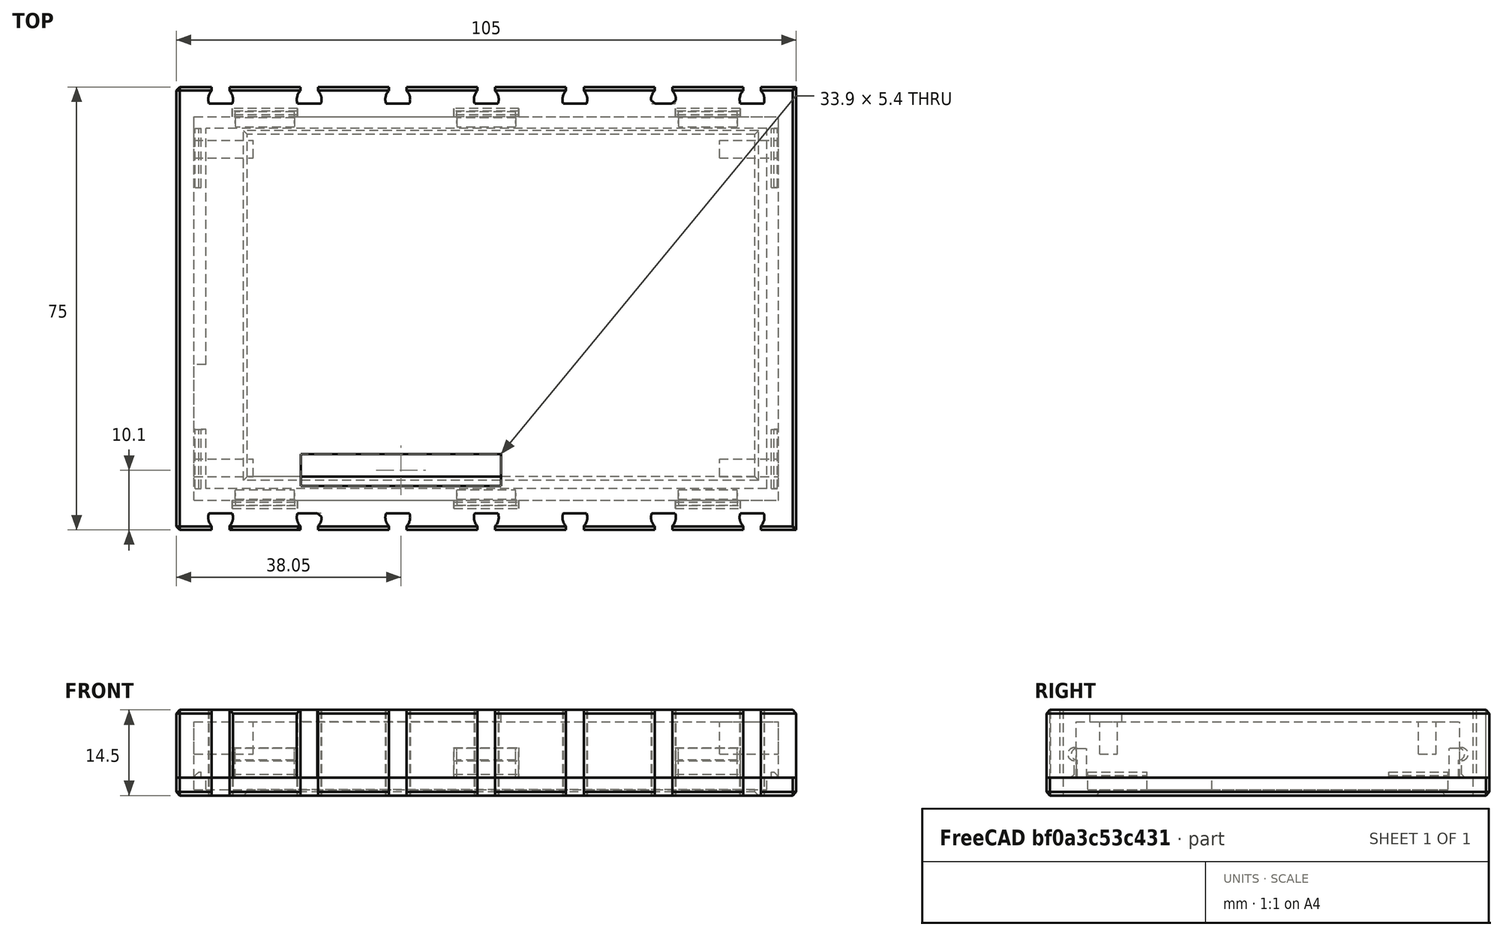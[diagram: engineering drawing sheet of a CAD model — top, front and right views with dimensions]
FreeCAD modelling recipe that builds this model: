
FCSTD DOCUMENT  (FreeCAD 0.19RUnknown)
Label: Display40
License: All rights reserved
LicenseURL: http://en.wikipedia.org/wiki/All_rights_reserved
objects: Part::Box×55, Part::MultiFuse×45, Part::Cylinder×26, Part::Cut×20, Part::Chamfer×3
note: 149 computed .brp shape members not serialized (recipe doc carries the construction recipe); baked Part::Feature solids carry a one-line shape summary decoded from their .brp

FEATURE [Part::Box] Box  label="Displ_base"
  AttacherType = Attacher::AttachEngine3D
  Height = 6
  Length = 95
  Width = 61
FEATURE [Part::Box] Box001  label="Connector"
  AttacherType = Attacher::AttachEngine3D
  Height = 13.4
  Length = 33.9
  Placement = pos=(16.1,0.4,6) rot=(0,0,1;0rad)
  Width = 5.4
FEATURE [Part::Box] Box002  label="Ribbon wire"
  AttacherType = Attacher::AttachEngine3D
  Height = 6
  Length = 2
  Placement = pos=(-2,10,0) rot=(0,0,1;0rad)
  Width = 11
FEATURE [Part::Box] Box003  label="Screen"
  AttacherType = Attacher::AttachEngine3D
  Height = 6
  Length = 86
  Placement = pos=(7,2,-3) rot=(0,0,1;0rad)
  Width = 58
FEATURE [Part::MultiFuse] Fusion  label="Display dummy"
  Shapes = -> [Box,Box001,Box003,Box002]
FEATURE [Part::Box] Box004  label="Displ_base001"
  AttacherType = Attacher::AttachEngine3D
  Height = 3
  Length = 105
  Placement = pos=(-5,-7,-1) rot=(0,0,1;0rad)
  Width = 75
FEATURE [Part::Cut] Cut
  Base = -> Box004
  Tool = -> Fusion
FEATURE [Part::Box] Box005  label="Displ_base002"
  AttacherType = Attacher::AttachEngine3D
  Height = 11.5
  Length = 105
  Placement = pos=(-5,-7,2) rot=(0,0,1;0rad)
  Width = 75
FEATURE [Part::Box] Box006  label="Displ_base003"
  AttacherType = Attacher::AttachEngine3D
  Height = 9.5
  Length = 99
  Placement = pos=(-2,-2,2) rot=(0,0,1;0rad)
  Width = 65
FEATURE [Part::Cut] Cut001
  Base = -> Box005
  Tool = -> Box006
FEATURE [Part::Cut] Cut002
  Base = -> Cut001
  Tool = -> Fusion
FEATURE [Part::Cylinder] Cylinder  label="bohrung"
  Angle = 360
  AttacherType = Attacher::AttachEngine3D
  Height = 25
  Placement = pos=(0,0,0) rot=(1,0,0;1.5708rad)
  Radius = 2.1
FEATURE [Part::Box] Box007  label="Nut 3x25x2"
  AttacherType = Attacher::AttachEngine3D
  Height = 2
  Length = 3
  Placement = pos=(6,0,0) rot=(0,0,1;0rad)
  Width = 25
FEATURE [Part::Box] Box008  label="Abflachung"
  AttacherType = Attacher::AttachEngine3D
  Height = 2
  Length = 4
  Placement = pos=(-2,-25,0.7) rot=(0,0,1;0rad)
  Width = 25
FEATURE [Part::Cut] Cut003  label="Kreisnut 4x25"
  Base = -> Cylinder
  Placement = pos=(7.5,25,2.1) rot=(0,0,1;0rad)
  Tool = -> Box008
FEATURE [Part::MultiFuse] Fusion001
  Placement = pos=(-5,68,-5) rot=(1,0,0;1.5708rad)
  Shapes = -> [Box007,Cut003]
FEATURE [Part::Box] Box009  label="Abflachung001"
  AttacherType = Attacher::AttachEngine3D
  Height = 2
  Length = 4
  Placement = pos=(-2,-25,0.7) rot=(0,0,1;0rad)
  Width = 25
FEATURE [Part::Box] Box010  label="Nut 3x25x003"
  AttacherType = Attacher::AttachEngine3D
  Height = 2
  Length = 3
  Placement = pos=(6,0,0) rot=(0,0,1;0rad)
  Width = 25
FEATURE [Part::Cylinder] Cylinder001  label="bohrung001"
  Angle = 360
  AttacherType = Attacher::AttachEngine3D
  Height = 25
  Placement = pos=(0,0,0) rot=(1,0,0;1.5708rad)
  Radius = 2.1
FEATURE [Part::Cut] Cut004  label="Kreisnut 4x026"
  Base = -> Cylinder001
  Placement = pos=(7.5,25,2.1) rot=(0,0,1;0rad)
  Tool = -> Box009
FEATURE [Part::MultiFuse] Fusion002
  Placement = pos=(10,68,-5) rot=(1,0,0;1.5708rad)
  Shapes = -> [Box010,Cut004]
FEATURE [Part::Box] Box011  label="Abflachung002"
  AttacherType = Attacher::AttachEngine3D
  Height = 2
  Length = 4
  Placement = pos=(-2,-25,0.7) rot=(0,0,1;0rad)
  Width = 25
FEATURE [Part::Box] Box012  label="Nut 3x25x004"
  AttacherType = Attacher::AttachEngine3D
  Height = 2
  Length = 3
  Placement = pos=(6,0,0) rot=(0,0,1;0rad)
  Width = 25
FEATURE [Part::Cylinder] Cylinder002  label="bohrung002"
  Angle = 360
  AttacherType = Attacher::AttachEngine3D
  Height = 25
  Placement = pos=(0,0,0) rot=(1,0,0;1.5708rad)
  Radius = 2.1
FEATURE [Part::Cut] Cut005  label="Kreisnut 4x027"
  Base = -> Cylinder002
  Placement = pos=(7.5,25,2.1) rot=(0,0,1;0rad)
  Tool = -> Box011
FEATURE [Part::MultiFuse] Fusion003
  Placement = pos=(25,68,-5) rot=(1,0,0;1.5708rad)
  Shapes = -> [Box012,Cut005]
FEATURE [Part::Box] Box013  label="Abflachung003"
  AttacherType = Attacher::AttachEngine3D
  Height = 2
  Length = 4
  Placement = pos=(-2,-25,0.7) rot=(0,0,1;0rad)
  Width = 25
FEATURE [Part::Box] Box014  label="Nut 3x25x005"
  AttacherType = Attacher::AttachEngine3D
  Height = 2
  Length = 3
  Placement = pos=(6,0,0) rot=(0,0,1;0rad)
  Width = 25
FEATURE [Part::Cylinder] Cylinder003  label="bohrung003"
  Angle = 360
  AttacherType = Attacher::AttachEngine3D
  Height = 25
  Placement = pos=(0,0,0) rot=(1,0,0;1.5708rad)
  Radius = 2.1
FEATURE [Part::Cut] Cut006  label="Kreisnut 4x028"
  Base = -> Cylinder003
  Placement = pos=(7.5,25,2.1) rot=(0,0,1;0rad)
  Tool = -> Box013
FEATURE [Part::MultiFuse] Fusion004
  Placement = pos=(40,68,-5) rot=(1,0,0;1.5708rad)
  Shapes = -> [Box014,Cut006]
FEATURE [Part::Box] Box015  label="Abflachung004"
  AttacherType = Attacher::AttachEngine3D
  Height = 2
  Length = 4
  Placement = pos=(-2,-25,0.7) rot=(0,0,1;0rad)
  Width = 25
FEATURE [Part::Box] Box016  label="Nut 3x25x006"
  AttacherType = Attacher::AttachEngine3D
  Height = 2
  Length = 3
  Placement = pos=(6,0,0) rot=(0,0,1;0rad)
  Width = 25
FEATURE [Part::Cylinder] Cylinder004  label="bohrung004"
  Angle = 360
  AttacherType = Attacher::AttachEngine3D
  Height = 25
  Placement = pos=(0,0,0) rot=(1,0,0;1.5708rad)
  Radius = 2.1
FEATURE [Part::Cut] Cut007  label="Kreisnut 4x029"
  Base = -> Cylinder004
  Placement = pos=(7.5,25,2.1) rot=(0,0,1;0rad)
  Tool = -> Box015
FEATURE [Part::MultiFuse] Fusion005
  Placement = pos=(55,68,-5) rot=(1,0,0;1.5708rad)
  Shapes = -> [Box016,Cut007]
FEATURE [Part::Box] Box017  label="Nut 3x25x007"
  AttacherType = Attacher::AttachEngine3D
  Height = 2
  Length = 3
  Placement = pos=(6,0,0) rot=(0,0,1;0rad)
  Width = 25
FEATURE [Part::Box] Box018  label="Abflachung005"
  AttacherType = Attacher::AttachEngine3D
  Height = 2
  Length = 4
  Placement = pos=(-2,-25,0.7) rot=(0,0,1;0rad)
  Width = 25
FEATURE [Part::Cylinder] Cylinder005  label="bohrung005"
  Angle = 360
  AttacherType = Attacher::AttachEngine3D
  Height = 25
  Placement = pos=(0,0,0) rot=(1,0,0;1.5708rad)
  Radius = 2.1
FEATURE [Part::Cut] Cut008  label="Kreisnut 4x030"
  Base = -> Cylinder005
  Placement = pos=(7.5,25,2.1) rot=(0,0,1;0rad)
  Tool = -> Box018
FEATURE [Part::MultiFuse] Fusion006
  Placement = pos=(70,68,-5) rot=(1,0,0;1.5708rad)
  Shapes = -> [Box017,Cut008]
FEATURE [Part::Box] Box019  label="Nut 3x25x008"
  AttacherType = Attacher::AttachEngine3D
  Height = 2
  Length = 3
  Placement = pos=(6,0,0) rot=(0,0,1;0rad)
  Width = 25
FEATURE [Part::Box] Box020  label="Abflachung006"
  AttacherType = Attacher::AttachEngine3D
  Height = 2
  Length = 4
  Placement = pos=(-2,-25,0.7) rot=(0,0,1;0rad)
  Width = 25
FEATURE [Part::Cylinder] Cylinder006  label="bohrung006"
  Angle = 360
  AttacherType = Attacher::AttachEngine3D
  Height = 25
  Placement = pos=(0,0,0) rot=(1,0,0;1.5708rad)
  Radius = 2.1
FEATURE [Part::Cut] Cut009  label="Kreisnut 4x031"
  Base = -> Cylinder006
  Placement = pos=(7.5,25,2.1) rot=(0,0,1;0rad)
  Tool = -> Box020
FEATURE [Part::MultiFuse] Fusion007
  Placement = pos=(85,68,-5) rot=(1,0,0;1.5708rad)
  Shapes = -> [Box019,Cut009]
FEATURE [Part::MultiFuse] Fusion008  label="Nuten01"
  Shapes = -> [Fusion007,Fusion006,Fusion003,Fusion005,Fusion002,Fusion001,Fusion004]
FEATURE [Part::Box] Box021  label="Nut 3x25x009"
  AttacherType = Attacher::AttachEngine3D
  Height = 2
  Length = 3
  Placement = pos=(6,0,0) rot=(0,0,1;0rad)
  Width = 25
FEATURE [Part::Box] Box022  label="Nut 3x25x010"
  AttacherType = Attacher::AttachEngine3D
  Height = 2
  Length = 3
  Placement = pos=(6,0,0) rot=(0,0,1;0rad)
  Width = 25
FEATURE [Part::Box] Box023  label="Abflachung007"
  AttacherType = Attacher::AttachEngine3D
  Height = 2
  Length = 4
  Placement = pos=(-2,-25,0.7) rot=(0,0,1;0rad)
  Width = 25
FEATURE [Part::Box] Box024  label="Abflachung008"
  AttacherType = Attacher::AttachEngine3D
  Height = 2
  Length = 4
  Placement = pos=(-2,-25,0.7) rot=(0,0,1;0rad)
  Width = 25
FEATURE [Part::Box] Box025  label="Abflachung009"
  AttacherType = Attacher::AttachEngine3D
  Height = 2
  Length = 4
  Placement = pos=(-2,-25,0.7) rot=(0,0,1;0rad)
  Width = 25
FEATURE [Part::Box] Box026  label="Abflachung010"
  AttacherType = Attacher::AttachEngine3D
  Height = 2
  Length = 4
  Placement = pos=(-2,-25,0.7) rot=(0,0,1;0rad)
  Width = 25
FEATURE [Part::Box] Box027  label="Nut 3x25x011"
  AttacherType = Attacher::AttachEngine3D
  Height = 2
  Length = 3
  Placement = pos=(6,0,0) rot=(0,0,1;0rad)
  Width = 25
FEATURE [Part::Box] Box028  label="Nut 3x25x012"
  AttacherType = Attacher::AttachEngine3D
  Height = 2
  Length = 3
  Placement = pos=(6,0,0) rot=(0,0,1;0rad)
  Width = 25
FEATURE [Part::Cylinder] Cylinder007  label="bohrung007"
  Angle = 360
  AttacherType = Attacher::AttachEngine3D
  Height = 25
  Placement = pos=(0,0,0) rot=(1,0,0;1.5708rad)
  Radius = 2.1
FEATURE [Part::Cut] Cut012  label="Kreisnut 4x034"
  Base = -> Cylinder007
  Placement = pos=(7.5,25,2.1) rot=(0,0,1;0rad)
  Tool = -> Box024
FEATURE [Part::MultiFuse] Fusion013
  Placement = pos=(10,68,-5) rot=(1,0,0;1.5708rad)
  Shapes = -> [Box027,Cut012]
FEATURE [Part::Cylinder] Cylinder008  label="bohrung008"
  Angle = 360
  AttacherType = Attacher::AttachEngine3D
  Height = 25
  Placement = pos=(0,0,0) rot=(1,0,0;1.5708rad)
  Radius = 2.1
FEATURE [Part::Cut] Cut011  label="Kreisnut 4x033"
  Base = -> Cylinder008
  Placement = pos=(7.5,25,2.1) rot=(0,0,1;0rad)
  Tool = -> Box023
FEATURE [Part::MultiFuse] Fusion010
  Placement = pos=(25,68,-5) rot=(1,0,0;1.5708rad)
  Shapes = -> [Box021,Cut011]
FEATURE [Part::Cylinder] Cylinder009  label="bohrung009"
  Angle = 360
  AttacherType = Attacher::AttachEngine3D
  Height = 25
  Placement = pos=(0,0,0) rot=(1,0,0;1.5708rad)
  Radius = 2.1
FEATURE [Part::Cut] Cut010  label="Kreisnut 4x032"
  Base = -> Cylinder009
  Placement = pos=(7.5,25,2.1) rot=(0,0,1;0rad)
  Tool = -> Box025
FEATURE [Part::MultiFuse] Fusion014
  Placement = pos=(-5,68,-5) rot=(1,0,0;1.5708rad)
  Shapes = -> [Box028,Cut010]
FEATURE [Part::Box] Box029  label="Nut 3x25x013"
  AttacherType = Attacher::AttachEngine3D
  Height = 2
  Length = 3
  Placement = pos=(6,0,0) rot=(0,0,1;0rad)
  Width = 25
FEATURE [Part::Cylinder] Cylinder010  label="bohrung010"
  Angle = 360
  AttacherType = Attacher::AttachEngine3D
  Height = 25
  Placement = pos=(0,0,0) rot=(1,0,0;1.5708rad)
  Radius = 2.1
FEATURE [Part::Box] Box030  label="Abflachung011"
  AttacherType = Attacher::AttachEngine3D
  Height = 2
  Length = 4
  Placement = pos=(-2,-25,0.7) rot=(0,0,1;0rad)
  Width = 25
FEATURE [Part::Box] Box031  label="Abflachung012"
  AttacherType = Attacher::AttachEngine3D
  Height = 2
  Length = 4
  Placement = pos=(-2,-25,0.7) rot=(0,0,1;0rad)
  Width = 25
FEATURE [Part::Cylinder] Cylinder011  label="bohrung011"
  Angle = 360
  AttacherType = Attacher::AttachEngine3D
  Height = 25
  Placement = pos=(0,0,0) rot=(1,0,0;1.5708rad)
  Radius = 2.1
FEATURE [Part::Cut] Cut014  label="Kreisnut 4x036"
  Base = -> Cylinder011
  Placement = pos=(7.5,25,2.1) rot=(0,0,1;0rad)
  Tool = -> Box031
FEATURE [Part::MultiFuse] Fusion012
  Placement = pos=(55,68,-5) rot=(1,0,0;1.5708rad)
  Shapes = -> [Box029,Cut014]
FEATURE [Part::Cylinder] Cylinder012  label="bohrung012"
  Angle = 360
  AttacherType = Attacher::AttachEngine3D
  Height = 25
  Placement = pos=(0,0,0) rot=(1,0,0;1.5708rad)
  Radius = 2.1
FEATURE [Part::Cylinder] Cylinder013  label="bohrung013"
  Angle = 360
  AttacherType = Attacher::AttachEngine3D
  Height = 25
  Placement = pos=(0,0,0) rot=(1,0,0;1.5708rad)
  Radius = 2.1
FEATURE [Part::Box] Box032  label="Nut 3x25x014"
  AttacherType = Attacher::AttachEngine3D
  Height = 2
  Length = 3
  Placement = pos=(6,0,0) rot=(0,0,1;0rad)
  Width = 25
FEATURE [Part::Box] Box033  label="Abflachung013"
  AttacherType = Attacher::AttachEngine3D
  Height = 2
  Length = 4
  Placement = pos=(-2,-25,0.7) rot=(0,0,1;0rad)
  Width = 25
FEATURE [Part::Cut] Cut013  label="Kreisnut 4x035"
  Base = -> Cylinder013
  Placement = pos=(7.5,25,2.1) rot=(0,0,1;0rad)
  Tool = -> Box033
FEATURE [Part::MultiFuse] Fusion016
  Placement = pos=(85,68,-5) rot=(1,0,0;1.5708rad)
  Shapes = -> [Box032,Cut013]
FEATURE [Part::Box] Box034  label="Nut 3x25x015"
  AttacherType = Attacher::AttachEngine3D
  Height = 2
  Length = 3
  Placement = pos=(6,0,0) rot=(0,0,1;0rad)
  Width = 25
FEATURE [Part::Cut] Cut015  label="Kreisnut 4x037"
  Base = -> Cylinder012
  Placement = pos=(7.5,25,2.1) rot=(0,0,1;0rad)
  Tool = -> Box030
FEATURE [Part::MultiFuse] Fusion009
  Placement = pos=(70,68,-5) rot=(1,0,0;1.5708rad)
  Shapes = -> [Box034,Cut015]
FEATURE [Part::Cut] Cut016  label="Kreisnut 4x038"
  Base = -> Cylinder010
  Placement = pos=(7.5,25,2.1) rot=(0,0,1;0rad)
  Tool = -> Box026
FEATURE [Part::MultiFuse] Fusion015
  Placement = pos=(40,68,-5) rot=(1,0,0;1.5708rad)
  Shapes = -> [Box022,Cut016]
FEATURE [Part::MultiFuse] Fusion011  label="Nuten002"
  Placement = pos=(95,61,0) rot=(0,0,1;3.14159rad)
  Shapes = -> [Fusion016,Fusion009,Fusion010,Fusion012,Fusion013,Fusion014,Fusion015]
FEATURE [Part::MultiFuse] Fusion017  label="Nuten"
  Shapes = -> [Fusion008,Fusion011]
FEATURE [Part::Cut] Cut017
  Base = -> Cut
  Tool = -> Fusion017
FEATURE [Part::Cut] Cut018
  Base = -> Cut002
  Tool = -> Fusion017
FEATURE [Part::Box] Box035  label="Würfel"
  AttacherType = Attacher::AttachEngine3D
  Height = 5.5
  Length = 10
  Placement = pos=(0,2,6) rot=(0,0,1;0rad)
  Width = 3
FEATURE [Part::Box] Box036  label="Würfel001"
  AttacherType = Attacher::AttachEngine3D
  Height = 5.5
  Length = 10
  Placement = pos=(0,56,6) rot=(0,0,1;0rad)
  Width = 3
FEATURE [Part::MultiFuse] Fusion018
  Placement = pos=(-2,0,0) rot=(0,0,1;0rad)
  Shapes = -> [Box035,Box036]
FEATURE [Part::Box] Box037  label="Würfel002"
  AttacherType = Attacher::AttachEngine3D
  Height = 5.5
  Length = 10
  Placement = pos=(0,56,6) rot=(0,0,1;0rad)
  Width = 3
FEATURE [Part::Box] Box038  label="Würfel003"
  AttacherType = Attacher::AttachEngine3D
  Height = 5.5
  Length = 10
  Placement = pos=(0,2,6) rot=(0,0,1;0rad)
  Width = 3
FEATURE [Part::MultiFuse] Fusion019
  Placement = pos=(87,0,0) rot=(0,0,1;0rad)
  Shapes = -> [Box038,Box037]
FEATURE [Part::MultiFuse] Fusion020
  Shapes = -> [Fusion018,Fusion019]
FEATURE [Part::MultiFuse] Fusion021
  Shapes = -> [Cut018,Fusion020]
FEATURE [Part::Box] Box039  label="Würfel004"
  AttacherType = Attacher::AttachEngine3D
  Height = 5
  Length = 10
  Width = 1.6
FEATURE [Part::Cylinder] Cylinder014  label="Zylinder"
  Angle = 360
  AttacherType = Attacher::AttachEngine3D
  Height = 10
  Placement = pos=(0,0,4) rot=(0,1,0;1.5708rad)
  Radius = 1
FEATURE [Part::MultiFuse] Fusion022  label="clip"
  Placement = pos=(5,-1.8,2) rot=(0,0,1;0rad)
  Shapes = -> [Box039,Cylinder014]
FEATURE [Part::Cylinder] Cylinder015  label="Zylinder001"
  Angle = 360
  AttacherType = Attacher::AttachEngine3D
  Height = 11
  Placement = pos=(0,0,4) rot=(0,1,0;1.5708rad)
  Radius = 1.1
FEATURE [Part::Box] Box040  label="Würfel005"
  AttacherType = Attacher::AttachEngine3D
  Height = 5
  Length = 11
  Width = 1.6
FEATURE [Part::MultiFuse] Fusion023  label="neg_clip"
  Placement = pos=(4.5,-2,2) rot=(0,0,1;0rad)
  Shapes = -> [Box040,Cylinder015]
FEATURE [Part::Cylinder] Cylinder016  label="Zylinder002"
  Angle = 360
  AttacherType = Attacher::AttachEngine3D
  Height = 10
  Placement = pos=(0,0,4) rot=(0,1,0;1.5708rad)
  Radius = 1
FEATURE [Part::Box] Box041  label="Würfel006"
  AttacherType = Attacher::AttachEngine3D
  Height = 5
  Length = 10
  Width = 1.6
FEATURE [Part::MultiFuse] Fusion024  label="clip001"
  Placement = pos=(42.5,-1.8,2) rot=(0,0,1;0rad)
  Shapes = -> [Box041,Cylinder016]
FEATURE [Part::Box] Box042  label="Würfel007"
  AttacherType = Attacher::AttachEngine3D
  Height = 5
  Length = 10
  Width = 1.6
FEATURE [Part::Cylinder] Cylinder017  label="Zylinder003"
  Angle = 360
  AttacherType = Attacher::AttachEngine3D
  Height = 10
  Placement = pos=(0,0,4) rot=(0,1,0;1.5708rad)
  Radius = 1
FEATURE [Part::MultiFuse] Fusion025  label="clip002"
  Placement = pos=(80,-1.8,2) rot=(0,0,1;0rad)
  Shapes = -> [Box042,Cylinder017]
FEATURE [Part::MultiFuse] Fusion026  label="pos_clip"
  Shapes = -> [Fusion022,Fusion024,Fusion025]
FEATURE [Part::Box] Box043  label="Würfel008"
  AttacherType = Attacher::AttachEngine3D
  Height = 5
  Length = 11
  Width = 1.6
FEATURE [Part::Cylinder] Cylinder018  label="Zylinder004"
  Angle = 360
  AttacherType = Attacher::AttachEngine3D
  Height = 11
  Placement = pos=(0,0,4) rot=(0,1,0;1.5708rad)
  Radius = 1.1
FEATURE [Part::MultiFuse] Fusion027  label="neg_clip001"
  Placement = pos=(42,-2,2) rot=(0,0,1;0rad)
  Shapes = -> [Box043,Cylinder018]
FEATURE [Part::Box] Box044  label="Würfel009"
  AttacherType = Attacher::AttachEngine3D
  Height = 5
  Length = 11
  Width = 1.6
FEATURE [Part::Cylinder] Cylinder019  label="Zylinder005"
  Angle = 360
  AttacherType = Attacher::AttachEngine3D
  Height = 11
  Placement = pos=(0,0,4) rot=(0,1,0;1.5708rad)
  Radius = 1.1
FEATURE [Part::MultiFuse] Fusion028  label="neg_clip002"
  Placement = pos=(79.5,-2,2) rot=(0,0,1;0rad)
  Shapes = -> [Box044,Cylinder019]
FEATURE [Part::MultiFuse] Fusion029  label="neg_clip003"
  Placement = pos=(0,-0.3,0) rot=(0,0,1;0rad)
  Shapes = -> [Fusion023,Fusion027,Fusion028]
FEATURE [Part::Cylinder] Cylinder020  label="Zylinder006"
  Angle = 360
  AttacherType = Attacher::AttachEngine3D
  Height = 10
  Placement = pos=(0,0,4) rot=(0,1,0;1.5708rad)
  Radius = 1
FEATURE [Part::Cylinder] Cylinder021  label="Zylinder007"
  Angle = 360
  AttacherType = Attacher::AttachEngine3D
  Height = 10
  Placement = pos=(0,0,4) rot=(0,1,0;1.5708rad)
  Radius = 1
FEATURE [Part::Box] Box045  label="Würfel010"
  AttacherType = Attacher::AttachEngine3D
  Height = 5
  Length = 10
  Width = 1.6
FEATURE [Part::MultiFuse] Fusion033  label="clip005"
  Placement = pos=(80,-1.8,2) rot=(0,0,1;0rad)
  Shapes = -> [Box045,Cylinder021]
FEATURE [Part::Box] Box046  label="Würfel011"
  AttacherType = Attacher::AttachEngine3D
  Height = 5
  Length = 10
  Width = 1.6
FEATURE [Part::Cylinder] Cylinder022  label="Zylinder008"
  Angle = 360
  AttacherType = Attacher::AttachEngine3D
  Height = 10
  Placement = pos=(0,0,4) rot=(0,1,0;1.5708rad)
  Radius = 1
FEATURE [Part::MultiFuse] Fusion030  label="clip003"
  Placement = pos=(42.5,-1.8,2) rot=(0,0,1;0rad)
  Shapes = -> [Box046,Cylinder022]
FEATURE [Part::Box] Box047  label="Würfel012"
  AttacherType = Attacher::AttachEngine3D
  Height = 5
  Length = 10
  Width = 1.6
FEATURE [Part::MultiFuse] Fusion032  label="clip004"
  Placement = pos=(5,-1.8,2) rot=(0,0,1;0rad)
  Shapes = -> [Box047,Cylinder020]
FEATURE [Part::MultiFuse] Fusion031  label="pos_clip001"
  Placement = pos=(95,61,0) rot=(0,0,1;3.14159rad)
  Shapes = -> [Fusion032,Fusion030,Fusion033]
FEATURE [Part::MultiFuse] Fusion034
  Shapes = -> [Fusion031,Fusion026]
FEATURE [Part::Cylinder] Cylinder023  label="Zylinder009"
  Angle = 360
  AttacherType = Attacher::AttachEngine3D
  Height = 11
  Placement = pos=(0,0,4) rot=(0,1,0;1.5708rad)
  Radius = 1.1
FEATURE [Part::Box] Box048  label="Würfel013"
  AttacherType = Attacher::AttachEngine3D
  Height = 5
  Length = 11
  Width = 1.6
FEATURE [Part::Box] Box049  label="Würfel014"
  AttacherType = Attacher::AttachEngine3D
  Height = 5
  Length = 11
  Width = 1.6
FEATURE [Part::Cylinder] Cylinder024  label="Zylinder010"
  Angle = 360
  AttacherType = Attacher::AttachEngine3D
  Height = 11
  Placement = pos=(0,0,4) rot=(0,1,0;1.5708rad)
  Radius = 1.1
FEATURE [Part::MultiFuse] Fusion037  label="neg_clip006"
  Placement = pos=(42,-2,2) rot=(0,0,1;0rad)
  Shapes = -> [Box049,Cylinder024]
FEATURE [Part::Cylinder] Cylinder025  label="Zylinder011"
  Angle = 360
  AttacherType = Attacher::AttachEngine3D
  Height = 11
  Placement = pos=(0,0,4) rot=(0,1,0;1.5708rad)
  Radius = 1.1
FEATURE [Part::MultiFuse] Fusion035  label="neg_clip004"
  Placement = pos=(4.5,-2,2) rot=(0,0,1;0rad)
  Shapes = -> [Box048,Cylinder025]
FEATURE [Part::Box] Box050  label="Würfel015"
  AttacherType = Attacher::AttachEngine3D
  Height = 5
  Length = 11
  Width = 1.6
FEATURE [Part::MultiFuse] Fusion038  label="neg_clip007"
  Placement = pos=(79.5,-2,2) rot=(0,0,1;0rad)
  Shapes = -> [Box050,Cylinder023]
FEATURE [Part::MultiFuse] Fusion036  label="neg_clip005"
  Placement = pos=(95,61.3,0) rot=(0,0,1;3.14159rad)
  Shapes = -> [Fusion035,Fusion037,Fusion038]
FEATURE [Part::MultiFuse] Fusion039
  Shapes = -> [Fusion036,Fusion029]
FEATURE [Part::Cut] Cut019  label="Wanne"
  Base = -> Fusion021
  Tool = -> Fusion039
FEATURE [Part::MultiFuse] Fusion040
  Shapes = -> [Cut017,Fusion034]
FEATURE [Part::Box] Box051  label="Würfel016"
  AttacherType = Attacher::AttachEngine3D
  Height = 1
  Length = 1
  Placement = pos=(-1.8,0,2) rot=(0,0,1;0rad)
  Width = 10
FEATURE [Part::Box] Box052  label="Würfel017"
  AttacherType = Attacher::AttachEngine3D
  Height = 1
  Length = 1
  Placement = pos=(95.8,0,2) rot=(0,0,1;0rad)
  Width = 10
FEATURE [Part::MultiFuse] Fusion041
  Shapes = -> [Box051,Box052]
FEATURE [Part::Box] Box053  label="Würfel018"
  AttacherType = Attacher::AttachEngine3D
  Height = 1
  Length = 1
  Placement = pos=(-1.8,0,2) rot=(0,0,1;0rad)
  Width = 10
FEATURE [Part::Box] Box054  label="Würfel019"
  AttacherType = Attacher::AttachEngine3D
  Height = 1
  Length = 1
  Placement = pos=(95.8,0,2) rot=(0,0,1;0rad)
  Width = 10
FEATURE [Part::MultiFuse] Fusion042
  Placement = pos=(0,51,0) rot=(0,0,1;0rad)
  Shapes = -> [Box053,Box054]
FEATURE [Part::MultiFuse] Fusion043
  Shapes = -> [Fusion041,Fusion042]
FEATURE [Part::MultiFuse] Fusion044  label="Deckel"
  Shapes = -> [Fusion040,Fusion043]
FEATURE [Part::Chamfer] Chamfer  label="Deckel "
  Base = -> Fusion044
  Edges = 30 edges r=0.6: [Edge1,Edge3,Edge4,Edge5,Edge156,Edge164,Edge171,Edge178,Edge185,Edge192,Edge199,Edge206,Edge207,Edge208,Edge215,Edge222,Edge229,Edge236,Edge243,Edge250,Edge257,Edge258,Edge259,Edge260,Edge356,Edge358,Edge404,Edge414,Edge456,Edge464]
FEATURE [Part::Chamfer] Chamfer001  label="Wanne-Eickel... "
  Base = -> Cut019
  Edges = 26 edges r=0.6: [Edge1,Edge2,Edge3,Edge7,Edge8,Edge15,Edge22,Edge29,Edge36,Edge43,Edge50,Edge57,Edge58,Edge59,Edge66,Edge73,Edge80,Edge87,Edge94,Edge101,Edge280,Edge281,Edge331,Edge333,Edge335,Edge336]
FEATURE [Part::Chamfer] Chamfer002  label="Wanne final"
  Base = -> Chamfer001
  Edges = 6 edges r=0.6: [Edge115,Edge119,Edge123,Edge129,Edge133,Edge137]
